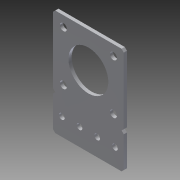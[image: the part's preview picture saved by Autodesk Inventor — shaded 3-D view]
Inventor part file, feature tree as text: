
AUTODESK INVENTOR PART (.ipt)
format: ipt  version: 2014 SP1 (Build 180222100, 222)  size: 163,840 bytes
history: native  units: in
note: dims shown in document units (in); Inventor stores cm internally (conversion verified against a paired STEP export)
features: other x1, extrude x1, imported_body x1, sketch x1
ambient origin geometry x8: Origin, YZ Plane, XZ Plane, XY Plane, X Axis, Y Axis, Z Axis, Center Point
bodies: Body1 (feature_tree)
feature tree (4):
  other  "Cut-Extrude1"
  extrude  "Extrusion1"  Depth=1.0in TaperAngle=0.0deg
  imported_body  "Base1"
  sketch  "Sketch1"  dims[d0=1.125in d1=1.0in d2=0.0in]
